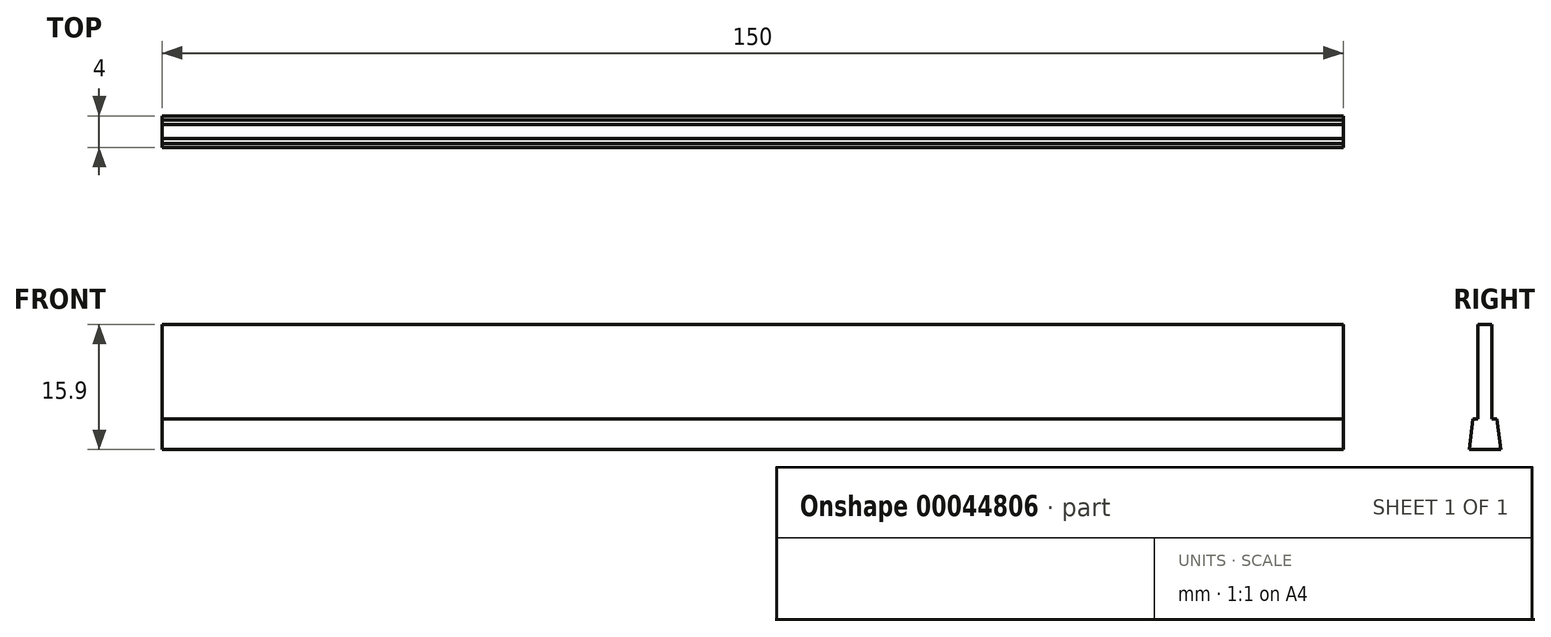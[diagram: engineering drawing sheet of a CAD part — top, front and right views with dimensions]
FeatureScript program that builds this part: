
annotation { "Feature Type Name" : "Feature", "Feature Type Description" : "" }
export const myFeature = defineFeature(function(context is Context, id is Id, definition is map)
    precondition{}
    {
        {
            var Q0;
            Q0=qCreatedBy(makeId("Right.planeOp"),FACE);
            var sketch = newSketch(context, id + "F0", { "sketchPlane" : qUnion([Q0])});
            skLineSegment(sketch, "E0.rect.bottom", {"start": v(0.9, 6) * mm, "end": v(-0.9, 6) * mm});
            skLineSegment(sketch, "E0.rect.top", {"start": v(0.9, -6) * mm, "end": v(-0.9, -6) * mm});
            skLineSegment(sketch, "E0.rect.left", {"start": v(0.9, 6) * mm, "end": v(0.9, -6) * mm});
            skLineSegment(sketch, "E0.rect.right", {"start": v(-0.9, 6) * mm, "end": v(-0.9, -6) * mm});
            skPoint(sketch, "E0.rect.middle", {"position": v(0, 0) * mm});
            skLineSegment(sketch, "E1.rect.bottom", {"start": v(2, -6) * mm, "end": v(-2, -6) * mm, "construction": true});
            skLineSegment(sketch, "E1.rect.top", {"start": v(2, -9.9) * mm, "end": v(-2, -9.9) * mm});
            skLineSegment(sketch, "E1.rect.left", {"start": v(2, -6) * mm, "end": v(2, -9.9) * mm, "construction": true});
            skLineSegment(sketch, "E1.rect.right", {"start": v(-2, -6) * mm, "end": v(-2, -9.9) * mm, "construction": true});
            skPoint(sketch, "E1.rect.middle", {"position": v(0, -7.95) * mm});
            skLineSegment(sketch, "E2", {"start": v(-1.5, -6) * mm, "end": v(1.5, -6) * mm});
            skPoint(sketch, "E3", {"position": v(0, -6) * mm});
            skLineSegment(sketch, "E4", {"start": v(-1.5, -6) * mm, "end": v(-2, -9.9) * mm});
            skLineSegment(sketch, "E5", {"start": v(1.5, -6) * mm, "end": v(2, -9.9) * mm});
            skLineSegment(sketch, "E6", {"start": v(-0.9, -6) * mm, "end": v(0.9, -6) * mm});
            skSolve(sketch);
        }
        {
            var Q0;
            Q0 = qSketchRegion(id + "F0", true);
            var Q1;
            Q1 = qConstructionFilter(qBodyType(qCreatedBy(id + "F0" ,EDGE), BodyType.WIRE), ConstructionObject.NO);
            extrude(context, id + "F1", {"entities" : qUnion([Q0]), "surfaceEntities" : qUnion([Q1]), "depth" : 150 * mm});
        }
    });
